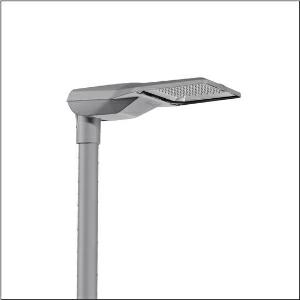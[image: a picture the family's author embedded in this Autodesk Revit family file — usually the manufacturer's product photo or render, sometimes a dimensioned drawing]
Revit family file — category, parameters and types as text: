
# Revit family: streetlight_sl_21_midi___pc-l_5xe7f33a08mb_bf39
name_source: partatom
category: Lighting Fixtures
units: mm (PartAtom-declared; Revit-internal decimal feet)

## family parameters
Cut with Voids When Loaded = No
Host = Face
Light Source = No
Part Type = Normal
Room Calculation Point = No
Round Connector Dimension = Use Diameter
Shared = No

## types (1)
- --- (1 x LED, 17390 lm, 136 W, 3000K)
    Apparent Load = 136 VA
    CIE Flux Codes = 38 78 98 100 100
    Color Rendering = 70
    Color Temperature = 3000K
    Default Elevation = 1800 mm
    Description = Streetlight SL 21 midi, mast luminaire, primary light control with lens, of PMMA, primary optical cover: cover, of toughened safety glass, transparent, light distribution: PC-L, light emission: direct distribution, primary light characteristic: asymmetric, left, installation type: post-top, side-entry, LED, 3G 1.5mm², High Power LED, rated luminous flux: 17.390lm, luminous efficacy: 128lm/W, light colour: 730, colour temperature: 3000K, control: overheat protection, constant luminous flux control, time-dependent luminous flux control, flexible luminous flux parameterisation, mains connection: 220..240V, AC, 50/60Hz, connection cable pre-assembled, cable length: 12,5m, wiring characteristics: H07RN-F, start of lifetime: 136W, end of service life: 142W, reduction: 61W, luminaire housing, of diecast aluminium, powder-coated, Siteco® metallic grey (DB 702S), corrosivity category C5 mid according to DIN EN ISO 12944, please order mast flange separately, inclination adjustable: 0°, 5°, 10°, 15°, sealing non-destructively replaceable, multi-level sealing system, length: 644mm, width: 335mm, height: 110mm, mast flange for spigot size: 42mm (side-entry): 5XC10008XM4, 60/48mm (side-entry/post-top): 5XC10108XM2, 76/60mm (side-entry/post-top): 5XC10108XM1, protection rating (complete): IP66, insulation class (complete): insulation class II (safety insulation), certification: CE, ENEC, ENEC+, VDE, impact resistance: IK09, permissible operating ambient temperature for outdoor applications: -40..+50°C, standard-compliant lighting for roads and squares, packaging unit: 1 piece

Light Distribution: PC-L
    Height = 111 mm
    Lamp = 1 x LED
    Lamp Light Flux = 17390 lm
    Lamp Power = 136 W
    Lamp count = 1
    Length = 644 mm
    Luminous efficacy = 128 lm/W
    Manufacturer = Siteco
    ModVariant = No
    Model = 5XE7F33A08MB
    Number of Poles = 1
    OnlyDefault = Yes
    Power Factor = 1
    Product Name = Streetlight SL 21 midi | PC-L
    Product group = mast luminaire | pylon top
    ProductGroupID = 6100
    Protection Class = Protection class II
    Protection Degree = IP 66
    RLX_Detail_Level = 1
    RLX_Emergency_Light_Flux = 0 lm
    RLX_Emergency_Type = 0
    RLX_Emergency_Type_DB = No
    RlxData = <blob elided: 93021 chars, md5=90940192>
    Socket = socket
    Standby Power = 0 W
    System Light Flux = 17390 lm
    System Power = 136 W
    Type Comments = factory setting: luminous flux: 100 % | Output Level: 100 % | 695 mA
    Type Image = l_1004298.jpg
    URL = http://relux.com
    VarID = @adj_032611
    Voltage = 0 V
    Weight = 0.00 kg
    Width = 336 mm

## geometry (parser evidence)
native form markers: Blend x4, Sweep x11
no freeform markers — native parametric forms only
